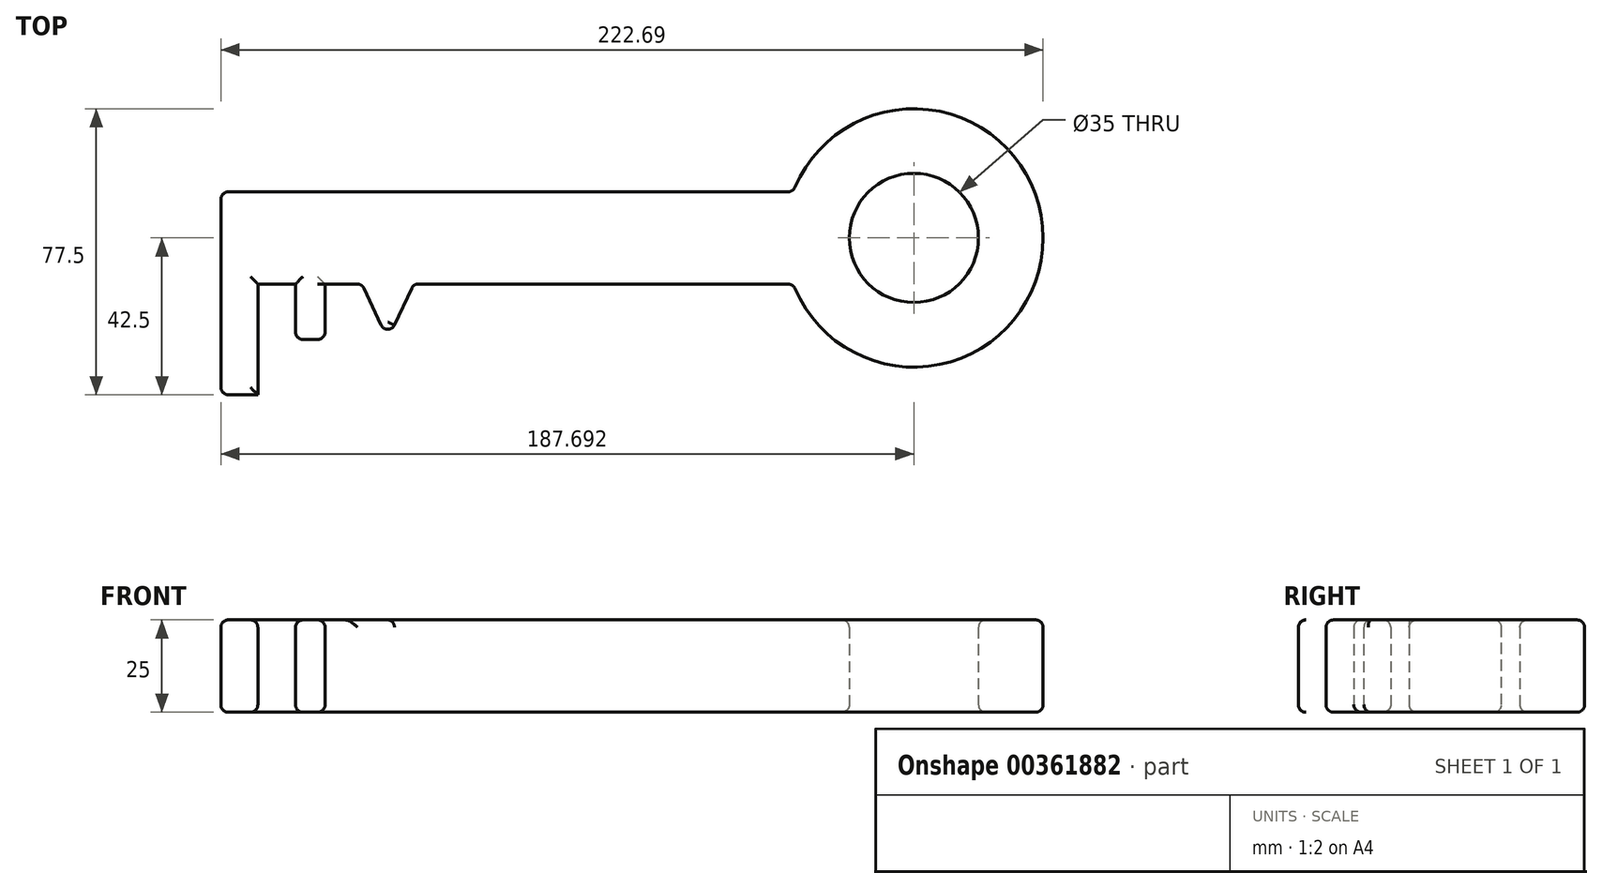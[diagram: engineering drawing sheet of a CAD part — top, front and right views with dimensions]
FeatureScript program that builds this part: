
annotation { "Feature Type Name" : "Feature", "Feature Type Description" : "" }
export const myFeature = defineFeature(function(context is Context, id is Id, definition is map)
    precondition{}
    {
        {
            var Q0;
            Q0=qCreatedBy(makeId("Top.planeOp"),FACE);
            var sketch = newSketch(context, id + "F0", { "sketchPlane" : qUnion([Q0])});
            skLineSegment(sketch, "E0.bottom", {"start": v(77.5, 12.5) * mm, "end": v(-77.5, 12.5) * mm});
            skLineSegment(sketch, "E0.top", {"start": v(77.5, -12.5) * mm, "end": v(-77.5, -12.5) * mm});
            skLineSegment(sketch, "E0.left", {"start": v(77.5, 12.5) * mm, "end": v(77.5, -12.5) * mm});
            skLineSegment(sketch, "E0.right", {"start": v(-77.5, 12.5) * mm, "end": v(-77.5, -12.5) * mm});
            skPoint(sketch, "E0.middle", {"position": v(0, 0) * mm});
            skLineSegment(sketch, "E1.bottom", {"start": v(-77.5, 12.5) * mm, "end": v(-77.5, 12.5) * mm});
            skLineSegment(sketch, "E1.top", {"start": v(-77.5, -12.5) * mm, "end": v(-77.5, -12.5) * mm});
            skPoint(sketch, "E1.middle", {"position": v(-77.5, 0) * mm});
            skLineSegment(sketch, "E2.bottom", {"start": v(-77.5, -12.5) * mm, "end": v(-67.5, -12.5) * mm});
            skLineSegment(sketch, "E2.top", {"start": v(-77.5, -42.5) * mm, "end": v(-67.5, -42.5) * mm});
            skLineSegment(sketch, "E2.left", {"start": v(-77.5, -12.5) * mm, "end": v(-77.5, -42.5) * mm});
            skLineSegment(sketch, "E2.right", {"start": v(-67.5, -12.5) * mm, "end": v(-67.5, -42.5) * mm});
            skLineSegment(sketch, "E3.bottom", {"start": v(-57.3, -12.5) * mm, "end": v(-49.3, -12.5) * mm});
            skLineSegment(sketch, "E3.top", {"start": v(-57.3, -27.5) * mm, "end": v(-49.3, -27.5) * mm});
            skLineSegment(sketch, "E3.left", {"start": v(-57.3, -12.5) * mm, "end": v(-57.3, -27.5) * mm});
            skLineSegment(sketch, "E3.right", {"start": v(-49.3, -12.5) * mm, "end": v(-49.3, -27.5) * mm});
            skLineSegment(sketch, "E4", {"start": v(-39.3, -12.5) * mm, "end": v(-32.3, -27.5) * mm});
            skLineSegment(sketch, "E5", {"start": v(-32.3, -27.5) * mm, "end": v(-25.3, -12.5) * mm});
            skLineSegment(sketch, "E6", {"start": v(-39.3, -12.5) * mm, "end": v(-25.3, -12.5) * mm});
            skLineSegment(sketch, "E7", {"start": v(-25.3, -12.5) * mm, "end": v(-39.3, -12.5) * mm});
            skArc(sketch, "E8", {"start": v(77.5, -12.5) * mm, "mid": v(145.2, 0) * mm, "end": v(77.5, 12.5) * mm});
            skCircle(sketch, "E9", {"center": v(110.2, 0) * mm, "radius": 17.5 * mm});
            skLineSegment(sketch, "E10", {"start": v(-77.5, 0) * mm, "end": v(110.2, 0) * mm, "construction": true});
            skSolve(sketch);
        }
        {
            var Q0;
            Q0 = qSketchRegion(id + "F0", true);
            extrude(context, id + "F1", {"entities" : qUnion([Q0]), "depth" : 25 * mm});
        }
        {
            var Q0;
            Q0=makeQuery(id+"F1.opExtrude","CAP_EDGE",EDGE,{"disambiguationData":[OSD([sQuery(id+"F0.wireOp",EDGE,"E0.bottom")])],"isStart":false});
            var Q1;
            Q1=makeQuery(id+"F1.opExtrude","CAP_EDGE",EDGE,{"disambiguationData":[OSD([sQuery(id+"F0.wireOp",EDGE,"E0.right"),sQuery(id+"F0.wireOp",EDGE,"E2.left")])],"isStart":false});
            var Q2;
            Q2=makeQuery(id+"F1.opExtrude","CAP_EDGE",EDGE,{"disambiguationData":[OSD([sQuery(id+"F0.wireOp",EDGE,"E2.right")])],"isStart":false});
            var Q3;
            Q3=makeQuery(id+"F1.opExtrude","CAP_EDGE",EDGE,{"disambiguationData":[OSD([sQuery(id+"F0.wireOp",EDGE,"E2.top")])],"isStart":false});
            var Q4;
            {var subQ0=sQuery(id+"F0.wireOp",EDGE,"E0.top");Q4=makeQuery(id+"F1.opExtrude","CAP_EDGE",EDGE,{"disambiguationData":[OSD([subQ0]),TDD([makeQuery(id+"F0.imprint","IMPRINT",EDGE,{"disambiguationData":[TD([[makeQuery(id+"F0.imprint","INTERSECT",VERTEX,{"derivedFrom":[subQ0,sQuery(id+"F0.wireOp",EDGE,"E2.bottom"),sQuery(id+"F0.wireOp",EDGE,"E2.right")]}),1.0]])],"derivedFrom":subQ0})])],"isStart":false});}
            var Q5;
            Q5=makeQuery(id+"F1.opExtrude","CAP_EDGE",EDGE,{"disambiguationData":[OSD([sQuery(id+"F0.wireOp",EDGE,"E3.left")])],"isStart":false});
            var Q6;
            Q6=makeQuery(id+"F1.opExtrude","CAP_EDGE",EDGE,{"disambiguationData":[OSD([sQuery(id+"F0.wireOp",EDGE,"E3.right")])],"isStart":false});
            var Q7;
            Q7=makeQuery(id+"F1.opExtrude","CAP_EDGE",EDGE,{"disambiguationData":[OSD([sQuery(id+"F0.wireOp",EDGE,"E3.top")])],"isStart":false});
            var Q8;
            Q8=makeQuery(id+"F1.opExtrude","CAP_EDGE",EDGE,{"disambiguationData":[OSD([sQuery(id+"F0.wireOp",EDGE,"E4")])],"isStart":false});
            var Q9;
            {var subQ0=sQuery(id+"F0.wireOp",EDGE,"E0.top");Q9=makeQuery(id+"F1.opExtrude","CAP_EDGE",EDGE,{"disambiguationData":[OSD([subQ0]),TDD([makeQuery(id+"F0.imprint","IMPRINT",EDGE,{"disambiguationData":[TD([[makeQuery(id+"F0.imprint","INTERSECT",VERTEX,{"derivedFrom":[subQ0,sQuery(id+"F0.wireOp",EDGE,"E0.left"),sQuery(id+"F0.wireOp",EDGE,"E8")]}),-1.0]])],"derivedFrom":subQ0})])],"isStart":false});}
            var Q10;
            Q10=makeQuery(id+"F1.opExtrude","CAP_EDGE",EDGE,{"disambiguationData":[OSD([sQuery(id+"F0.wireOp",EDGE,"E5")])],"isStart":false});
            var Q11;
            Q11=makeQuery(id+"F1.opExtrude","CAP_EDGE",EDGE,{"disambiguationData":[OSD([sQuery(id+"F0.wireOp",EDGE,"E8")])],"isStart":false});
            var Q12;
            Q12=makeQuery(id+"F1.opExtrude","CAP_EDGE",EDGE,{"disambiguationData":[OSD([sQuery(id+"F0.wireOp",EDGE,"E9")])],"isStart":false});
            var Q13;
            Q13=makeQuery(id+"F1.opExtrude","CAP_EDGE",EDGE,{"disambiguationData":[OSD([sQuery(id+"F0.wireOp",EDGE,"E8")])],"isStart":true});
            var Q14;
            Q14=makeQuery(id+"F1.opExtrude","SWEPT_EDGE",EDGE,{"disambiguationData":[OSD([sQuery(id+"F0.wireOp",EDGE,"E0.bottom"),sQuery(id+"F0.wireOp",EDGE,"E0.left"),sQuery(id+"F0.wireOp",EDGE,"E8")])]});
            var Q15;
            Q15=makeQuery(id+"F1.opExtrude","SWEPT_FACE",FACE,{"disambiguationData":[OSD([sQuery(id+"F0.wireOp",EDGE,"E8")])]});
            var Q16;
            Q16=makeQuery(id+"F1.opExtrude","SWEPT_FACE",FACE,{"disambiguationData":[OSD([sQuery(id+"F0.wireOp",EDGE,"E0.bottom")])]});
            var Q17;
            Q17=makeQuery(id+"F1.opExtrude","CAP_EDGE",EDGE,{"disambiguationData":[OSD([sQuery(id+"F0.wireOp",EDGE,"E9")])],"isStart":true});
            var Q18;
            {var subQ0=sQuery(id+"F0.wireOp",EDGE,"E0.top");Q18=makeQuery(id+"F1.opExtrude","CAP_EDGE",EDGE,{"disambiguationData":[OSD([subQ0]),TDD([makeQuery(id+"F0.imprint","IMPRINT",EDGE,{"disambiguationData":[TD([[makeQuery(id+"F0.imprint","INTERSECT",VERTEX,{"derivedFrom":[subQ0,sQuery(id+"F0.wireOp",EDGE,"E0.left"),sQuery(id+"F0.wireOp",EDGE,"E8")]}),-1.0]])],"derivedFrom":subQ0})])],"isStart":true});}
            var Q19;
            Q19=makeQuery(id+"F1.opExtrude","CAP_EDGE",EDGE,{"disambiguationData":[OSD([sQuery(id+"F0.wireOp",EDGE,"E5")])],"isStart":true});
            var Q20;
            {var subQ0=sQuery(id+"F0.wireOp",EDGE,"E0.top");Q20=makeQuery(id+"F1.opExtrude","CAP_EDGE",EDGE,{"disambiguationData":[OSD([subQ0]),TDD([makeQuery(id+"F0.imprint","IMPRINT",EDGE,{"disambiguationData":[TD([[makeQuery(id+"F0.imprint","INTERSECT",VERTEX,{"derivedFrom":[subQ0,sQuery(id+"F0.wireOp",EDGE,"E3.bottom"),sQuery(id+"F0.wireOp",EDGE,"E3.right")]}),1.0]])],"derivedFrom":subQ0})])],"isStart":true});}
            var Q21;
            Q21=makeQuery(id+"F1.opExtrude","CAP_EDGE",EDGE,{"disambiguationData":[OSD([sQuery(id+"F0.wireOp",EDGE,"E4")])],"isStart":true});
            var Q22;
            Q22=makeQuery(id+"F1.opExtrude","CAP_EDGE",EDGE,{"disambiguationData":[OSD([sQuery(id+"F0.wireOp",EDGE,"E3.right")])],"isStart":true});
            var Q23;
            Q23=makeQuery(id+"F1.opExtrude","CAP_EDGE",EDGE,{"disambiguationData":[OSD([sQuery(id+"F0.wireOp",EDGE,"E3.top")])],"isStart":true});
            var Q24;
            Q24=makeQuery(id+"F1.opExtrude","CAP_EDGE",EDGE,{"disambiguationData":[OSD([sQuery(id+"F0.wireOp",EDGE,"E3.left")])],"isStart":true});
            var Q25;
            {var subQ0=sQuery(id+"F0.wireOp",EDGE,"E0.top");Q25=makeQuery(id+"F1.opExtrude","CAP_EDGE",EDGE,{"disambiguationData":[OSD([subQ0]),TDD([makeQuery(id+"F0.imprint","IMPRINT",EDGE,{"disambiguationData":[TD([[makeQuery(id+"F0.imprint","INTERSECT",VERTEX,{"derivedFrom":[subQ0,sQuery(id+"F0.wireOp",EDGE,"E2.bottom"),sQuery(id+"F0.wireOp",EDGE,"E2.right")]}),1.0]])],"derivedFrom":subQ0})])],"isStart":true});}
            var Q26;
            Q26=makeQuery(id+"F1.opExtrude","CAP_EDGE",EDGE,{"disambiguationData":[OSD([sQuery(id+"F0.wireOp",EDGE,"E2.right")])],"isStart":true});
            var Q27;
            Q27=makeQuery(id+"F1.opExtrude","CAP_EDGE",EDGE,{"disambiguationData":[OSD([sQuery(id+"F0.wireOp",EDGE,"E0.right"),sQuery(id+"F0.wireOp",EDGE,"E2.left")])],"isStart":true});
            var Q28;
            Q28=makeQuery(id+"F1.opExtrude","SWEPT_EDGE",EDGE,{"disambiguationData":[OSD([sQuery(id+"F0.wireOp",EDGE,"E2.top"),sQuery(id+"F0.wireOp",EDGE,"E2.left")])]});
            var Q29;
            Q29=makeQuery(id+"F1.opExtrude","SWEPT_EDGE",EDGE,{"disambiguationData":[OSD([sQuery(id+"F0.wireOp",EDGE,"E4"),sQuery(id+"F0.wireOp",EDGE,"E5")])]});
            var Q30;
            Q30=makeQuery(id+"F1.opExtrude","SWEPT_EDGE",EDGE,{"disambiguationData":[OSD([sQuery(id+"F0.wireOp",EDGE,"E0.top"),sQuery(id+"F0.wireOp",EDGE,"E5"),sQuery(id+"F0.wireOp",EDGE,"E6")])]});
            var Q31;
            Q31=makeQuery(id+"F1.opExtrude","SWEPT_EDGE",EDGE,{"disambiguationData":[OSD([sQuery(id+"F0.wireOp",EDGE,"E0.top"),sQuery(id+"F0.wireOp",EDGE,"E4"),sQuery(id+"F0.wireOp",EDGE,"E6")])]});
            var Q32;
            Q32=makeQuery(id+"F1.opExtrude","SWEPT_FACE",FACE,{"disambiguationData":[OSD([sQuery(id+"F0.wireOp",EDGE,"E3.top")])]});
            var Q33;
            Q33=makeQuery(id+"F1.opExtrude","CAP_EDGE",EDGE,{"disambiguationData":[OSD([sQuery(id+"F0.wireOp",EDGE,"E2.top")])],"isStart":true});
            fillet(context, id + "F2", {"entities" : qUnion([Q0, Q1, Q2, Q3, Q4, Q5, Q6, Q7, Q8, Q9, Q10, Q11, Q12, Q13, Q14, Q15, Q16, Q17, Q18, Q19, Q20, Q21, Q22, Q23, Q24, Q25, Q26, Q27, Q28, Q29, Q30, Q31, Q32, Q33]), "radius" : 2 * mm, "tangentPropagation" : true, "allowEdgeOverflow" : false});
        }
    });
